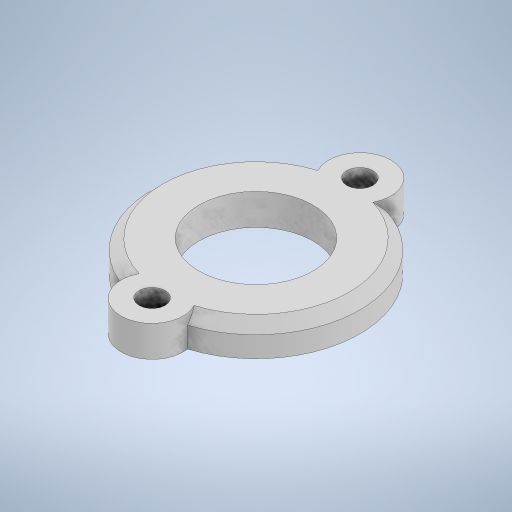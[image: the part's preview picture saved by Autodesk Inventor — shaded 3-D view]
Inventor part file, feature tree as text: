
AUTODESK INVENTOR PART (.ipt)
format: ipt  version: 2023 (Build 270158000, 158)  size: 259,584 bytes
history: native  units: mm
features: other x1, extrude x1, chamfer x1, sketch x1
ambient origin geometry x8: Origin, YZ Plane, XZ Plane, XY Plane, X Axis, Y Axis, Z Axis, Center Point
bodies: Body1 (feature_tree)
feature tree (4):
  other  "솔리드1"
  extrude  "돌출1"  Depth=20.0mm
  chamfer  "모따기1"  Distance=2.5mm
  sketch  "스케치1"
